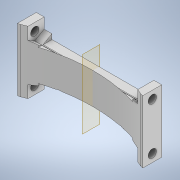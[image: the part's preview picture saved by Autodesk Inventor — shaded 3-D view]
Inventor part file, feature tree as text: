
AUTODESK INVENTOR PART (.ipt)
format: ipt  version: 2020 (Build 240168000, 168)  size: 292,864 bytes
history: native  units: in
note: dims shown in document units (in); Inventor stores cm internally (conversion verified against a paired STEP export)
features: sketch x7, extrude x5, plane x1, mirror x1, fillet x1, emboss x1
ambient origin geometry x8: Origin, YZ Plane, XZ Plane, XY Plane, X Axis, Y Axis, Z Axis, Center Point
bodies: Solid1 (feature_tree)
feature tree (16):
  extrude  "Extrusion1"  Depth=2.0in
  extrude  "Extrusion2"  Depth=0.5in
  extrude  "Extrusion3"  Depth=0.5in
  plane  "Work Plane1"
  mirror  "Mirror1"
  extrude  "Extrusion4"  Depth=0.25in
  fillet  "Fillet1"  Radius=0.25in
  emboss  "Emboss1"
  sketch  "Sketch6"  dims[d18=0.0in d19=0.0in]
  extrude  "Extrusion5"  Depth=1.5in
  sketch  "Sketch1"  dims[d0=4.0in d1=2.0in]
  sketch  "Sketch2"  dims[d2=1.0in d3=0.5in]
  sketch  "Sketch3"  dims[d4=0.5in d5=0.5in]
  sketch  "Sketch4"  dims[d6=0.6in d7=0.0in d8=0.3in d9=0.25in]
  sketch  "Sketch5"  dims[d10=0.2656in d11=0.7874in d13=1.5in d14=0.3937in d16=1.0in]
  sketch  "Sketch7"  dims[d20=0.4532in d21=0.25in d22=0.0in d23=5.2in d24=10.0in d25=0.0in d26=0.0in d27=0.25in d28=0.0354in d29=0.0in d30=2.0in d31=1.0in d32=0.75in d33=0.375in d34=0.6in d35=0.0in]
